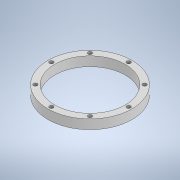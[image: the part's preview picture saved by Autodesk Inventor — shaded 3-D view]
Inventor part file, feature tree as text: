
AUTODESK INVENTOR PART (.ipt)
format: ipt  version: 2021 (Build 250183000, 183)  size: 131,072 bytes
history: native  units: mm
features: sketch x2, revolve x1, hole x1
ambient origin geometry x8: Origin, YZ Plane, XZ Plane, XY Plane, X Axis, Y Axis, Z Axis, Center Point
bodies: Solid1 (feature_tree)
feature tree (4):
  revolve  "Revolution1"  [1 undecoded]
  hole  "Hole1"  [1 undecoded]
  sketch  "Sketch1"  dims[d0=45.5mm d1=4.0mm]
  sketch  "Sketch2"  dims[d2=11.0mm d3=90.0deg d4=4.0mm d5=4.0mm d6=80.0mm d8=360.0deg d10=4.5mm d11=8.0mm d12=9.4mm d13=2.0mm d14=90.0deg d15=11.8mm d16=20.594885mm]
note: 2 required parameter values undecoded (feature->parameter linkage not recoverable at this tier; creation-order binding heuristic only, values carry confidence <= 0.55)